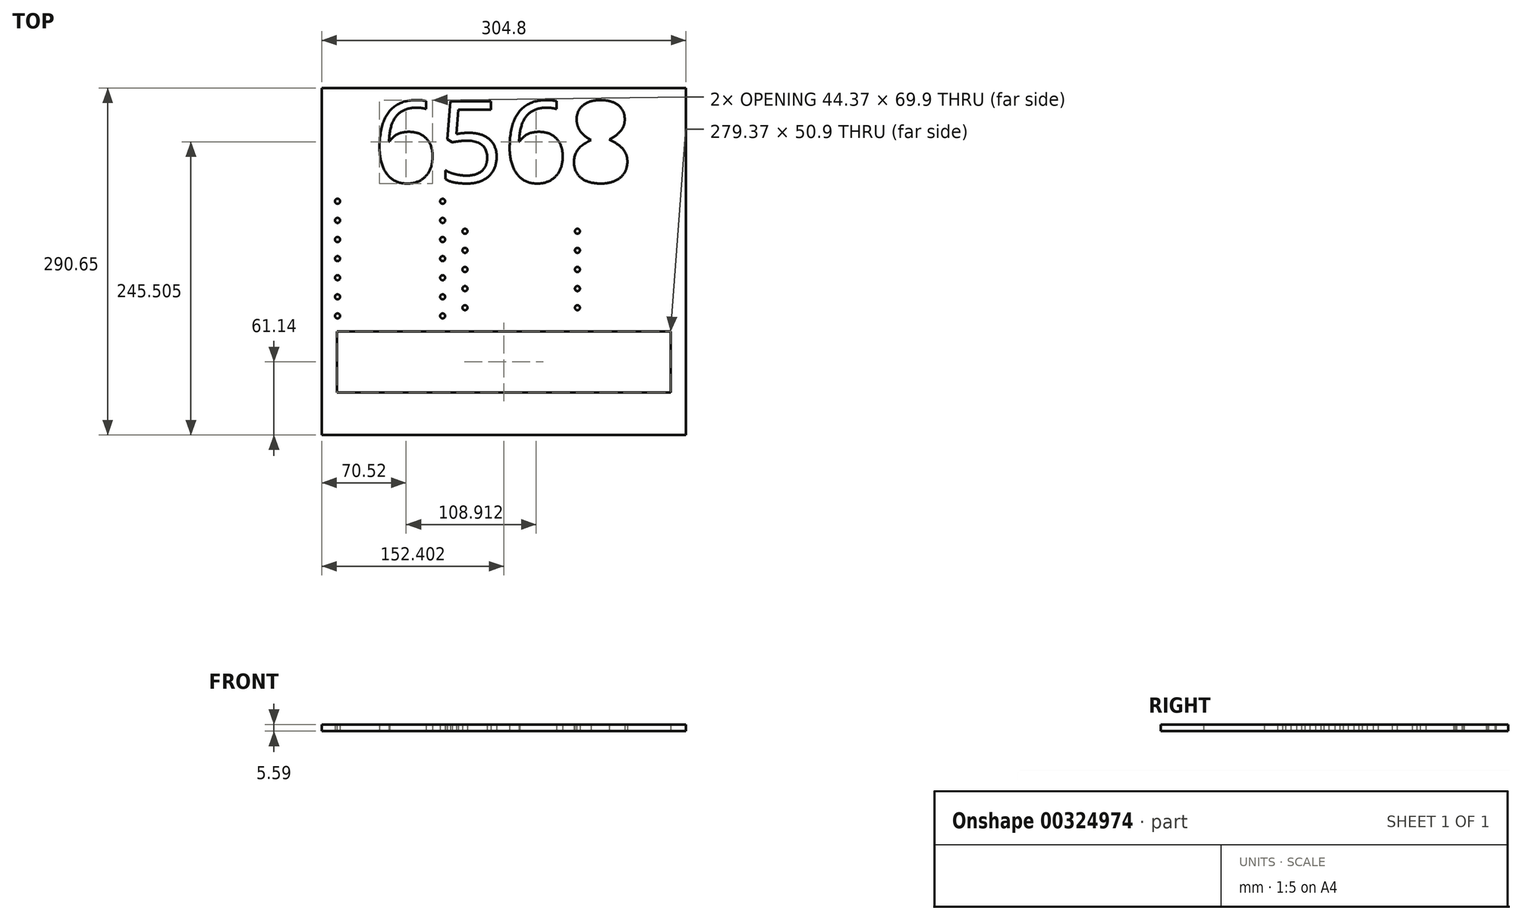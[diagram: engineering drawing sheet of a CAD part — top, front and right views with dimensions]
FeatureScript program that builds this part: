
annotation { "Feature Type Name" : "Feature", "Feature Type Description" : "" }
export const myFeature = defineFeature(function(context is Context, id is Id, definition is map)
    precondition{}
    {
        {
            var Q0;
            Q0=qCreatedBy(makeId("Top.planeOp"),FACE);
            var sketch = newSketch(context, id + "F0", { "sketchPlane" : qUnion([Q0])});
            skLineSegment(sketch, "E0.top", {"start": v(-150.79, -86.6) * mm, "end": v(154.01, -86.6) * mm});
            skLineSegment(sketch, "E0.left", {"start": v(-150.79, 204.06) * mm, "end": v(-150.79, -86.6) * mm});
            skLineSegment(sketch, "E0.right", {"start": v(154.01, 204.06) * mm, "end": v(154.01, -86.6) * mm});
            skLineSegment(sketch, "E1", {"start": v(-138.07, -50.9) * mm, "end": v(-138.07, 0) * mm});
            skLineSegment(sketch, "E2", {"start": v(141.3, -50.9) * mm, "end": v(141.3, 0) * mm});
            skLineSegment(sketch, "E3", {"start": v(-138.07, 0) * mm, "end": v(141.3, 0) * mm});
            skLineSegment(sketch, "E4", {"start": v(-138.07, -50.9) * mm, "end": v(141.3, -50.9) * mm});
            skCircle(sketch, "E5", {"center": v(-137.64, 13.08) * mm, "radius": 2.1 * mm});
            skPoint(sketch, "E5.first.point", {"position": v(-137.67, 15.18) * mm});
            skPoint(sketch, "E5.second.point", {"position": v(-135.54, 13.06) * mm});
            skPoint(sketch, "E5.third.point", {"position": v(-138.07, 11.03) * mm});
            skCircle(sketch, "E6", {"center": v(-137.64, 29.08) * mm, "radius": 2.1 * mm});
            skPoint(sketch, "E6.first.point", {"position": v(-137.68, 31.18) * mm});
            skPoint(sketch, "E6.second.point", {"position": v(-135.62, 28.5) * mm});
            skPoint(sketch, "E6.third.point", {"position": v(-139.13, 27.6) * mm});
            skCircle(sketch, "E7", {"center": v(-137.63, 45.09) * mm, "radius": 2.1 * mm});
            skPoint(sketch, "E7.first.point", {"position": v(-137.64, 47.18) * mm});
            skPoint(sketch, "E7.second.point", {"position": v(-138.72, 46.88) * mm});
            skPoint(sketch, "E7.third.point", {"position": v(-136.8, 43.16) * mm});
            skCircle(sketch, "E8", {"center": v(-137.63, 61.08) * mm, "radius": 2.1 * mm});
            skPoint(sketch, "E8.first.point", {"position": v(-137.63, 63.18) * mm});
            skPoint(sketch, "E8.second.point", {"position": v(-138.89, 62.76) * mm});
            skPoint(sketch, "E8.third.point", {"position": v(-136.93, 59.1) * mm});
            skCircle(sketch, "E9", {"center": v(-137.64, 77.07) * mm, "radius": 2.1 * mm});
            skPoint(sketch, "E9.first.point", {"position": v(-138.72, 78.88) * mm});
            skPoint(sketch, "E9.second.point", {"position": v(-139.12, 78.57) * mm});
            skPoint(sketch, "E9.third.point", {"position": v(-136.52, 75.3) * mm});
            skCircle(sketch, "E10", {"center": v(-137.63, 93.09) * mm, "radius": 2.1 * mm});
            skPoint(sketch, "E10.first.point", {"position": v(-139.31, 94.34) * mm});
            skPoint(sketch, "E10.second.point", {"position": v(-139.56, 93.92) * mm});
            skPoint(sketch, "E10.third.point", {"position": v(-136.07, 91.68) * mm});
            skCircle(sketch, "E11", {"center": v(-137.63, 109.11) * mm, "radius": 2.11 * mm});
            skPoint(sketch, "E11.first.point", {"position": v(-139.7, 108.7) * mm});
            skPoint(sketch, "E11.second.point", {"position": v(-139.64, 108.48) * mm});
            skPoint(sketch, "E11.third.point", {"position": v(-135.74, 108.18) * mm});
            skCircle(sketch, "E12", {"center": v(-49.63, 109.08) * mm, "radius": 2.1 * mm});
            skPoint(sketch, "E12.first.point", {"position": v(-50.34, 107.1) * mm});
            skPoint(sketch, "E12.second.point", {"position": v(-48.8, 107.15) * mm});
            skPoint(sketch, "E12.third.point", {"position": v(-49.24, 111.15) * mm});
            skCircle(sketch, "E13", {"center": v(-49.63, 93.08) * mm, "radius": 2.1 * mm});
            skPoint(sketch, "E13.first.point", {"position": v(-49.3, 95.16) * mm});
            skPoint(sketch, "E13.second.point", {"position": v(-51.64, 92.47) * mm});
            skPoint(sketch, "E13.third.point", {"position": v(-49.1, 91.05) * mm});
            skCircle(sketch, "E14", {"center": v(-49.63, 77.08) * mm, "radius": 2.1 * mm});
            skPoint(sketch, "E14.first.point", {"position": v(-49.56, 74.99) * mm});
            skPoint(sketch, "E14.second.point", {"position": v(-48.67, 78.95) * mm});
            skPoint(sketch, "E14.third.point", {"position": v(-51.72, 77.28) * mm});
            skCircle(sketch, "E15", {"center": v(-49.63, 61.08) * mm, "radius": 2.1 * mm});
            skPoint(sketch, "E15.first.point", {"position": v(-49.36, 63.17) * mm});
            skPoint(sketch, "E15.second.point", {"position": v(-47.7, 61.89) * mm});
            skPoint(sketch, "E15.third.point", {"position": v(-51.3, 59.81) * mm});
            skCircle(sketch, "E16", {"center": v(-49.63, 45.08) * mm, "radius": 2.1 * mm});
            skPoint(sketch, "E16.first.point", {"position": v(-49.58, 47.18) * mm});
            skPoint(sketch, "E16.second.point", {"position": v(-47.57, 45.49) * mm});
            skPoint(sketch, "E16.third.point", {"position": v(-49.93, 43) * mm});
            skCircle(sketch, "E17", {"center": v(-49.63, 29.08) * mm, "radius": 2.1 * mm});
            skPoint(sketch, "E17.first.point", {"position": v(-48.52, 30.87) * mm});
            skPoint(sketch, "E17.second.point", {"position": v(-51.47, 30.1) * mm});
            skPoint(sketch, "E17.third.point", {"position": v(-49.04, 27.07) * mm});
            skCircle(sketch, "E18", {"center": v(-49.63, 13.08) * mm, "radius": 2.1 * mm});
            skPoint(sketch, "E18.first.point", {"position": v(-48.44, 14.81) * mm});
            skPoint(sketch, "E18.second.point", {"position": v(-51.72, 12.9) * mm});
            skPoint(sketch, "E18.third.point", {"position": v(-49.41, 11) * mm});
            skCircle(sketch, "E19", {"center": v(-30.95, 83.97) * mm, "radius": 2.1 * mm});
            skPoint(sketch, "E19.first.point", {"position": v(-32.05, 85.77) * mm});
            skPoint(sketch, "E19.second.point", {"position": v(-31.38, 81.92) * mm});
            skPoint(sketch, "E19.third.point", {"position": v(-28.96, 84.64) * mm});
            skCircle(sketch, "E20", {"center": v(-30.95, 67.97) * mm, "radius": 2.1 * mm});
            skPoint(sketch, "E20.first.point", {"position": v(-30.95, 70.07) * mm});
            skPoint(sketch, "E20.second.point", {"position": v(-32.65, 66.74) * mm});
            skPoint(sketch, "E20.third.point", {"position": v(-29.85, 66.18) * mm});
            skCircle(sketch, "E21", {"center": v(-30.95, 51.97) * mm, "radius": 2.1 * mm});
            skPoint(sketch, "E21.first.point", {"position": v(-33.05, 51.97) * mm});
            skPoint(sketch, "E21.first.point.positionSnap0", {"position": v(-34.95, 51.97) * mm});
            skPoint(sketch, "E21.second.point", {"position": v(-29.85, 50.18) * mm});
            skPoint(sketch, "E21.third.point", {"position": v(-29.85, 53.76) * mm});
            skCircle(sketch, "E22", {"center": v(-30.95, 35.97) * mm, "radius": 2.1 * mm});
            skPoint(sketch, "E22.first.point", {"position": v(-32.98, 36.49) * mm});
            skPoint(sketch, "E22.second.point", {"position": v(-32.03, 34.17) * mm});
            skPoint(sketch, "E22.third.point", {"position": v(-29.85, 37.76) * mm});
            skCircle(sketch, "E23", {"center": v(-30.95, 19.97) * mm, "radius": 2.1 * mm});
            skPoint(sketch, "E23.first.point", {"position": v(-32.6, 21.27) * mm});
            skPoint(sketch, "E23.second.point", {"position": v(-30.95, 17.87) * mm});
            skPoint(sketch, "E23.third.point", {"position": v(-28.85, 19.97) * mm});
            skCircle(sketch, "E24", {"center": v(63.19, 83.97) * mm, "radius": 2.1 * mm});
            skPoint(sketch, "E24.first.point", {"position": v(62.1, 85.77) * mm});
            skPoint(sketch, "E24.second.point", {"position": v(62.76, 81.92) * mm});
            skPoint(sketch, "E24.third.point", {"position": v(65.18, 84.64) * mm});
            skCircle(sketch, "E25", {"center": v(63.19, 67.97) * mm, "radius": 2.1 * mm});
            skPoint(sketch, "E25.first.point", {"position": v(63.19, 70.07) * mm});
            skPoint(sketch, "E25.second.point", {"position": v(61.49, 66.74) * mm});
            skPoint(sketch, "E25.third.point", {"position": v(64.29, 66.18) * mm});
            skCircle(sketch, "E26", {"center": v(63.2, 51.97) * mm, "radius": 2.1 * mm});
            skPoint(sketch, "E26.first.point", {"position": v(61.1, 51.97) * mm});
            skPoint(sketch, "E26.first.point.positionSnap0", {"position": v(59.2, 51.97) * mm});
            skPoint(sketch, "E26.second.point", {"position": v(64.29, 50.18) * mm});
            skPoint(sketch, "E26.third.point", {"position": v(64.29, 53.76) * mm});
            skCircle(sketch, "E27", {"center": v(63.2, 35.97) * mm, "radius": 2.1 * mm});
            skPoint(sketch, "E27.first.point", {"position": v(61.16, 36.49) * mm});
            skPoint(sketch, "E27.second.point", {"position": v(62.1, 34.17) * mm});
            skPoint(sketch, "E27.third.point", {"position": v(64.29, 37.76) * mm});
            skCircle(sketch, "E28", {"center": v(63.2, 19.97) * mm, "radius": 2.1 * mm});
            skPoint(sketch, "E28.first.point", {"position": v(61.54, 21.27) * mm});
            skPoint(sketch, "E28.second.point", {"position": v(63.19, 17.87) * mm});
            skPoint(sketch, "E28.third.point", {"position": v(65.3, 19.97) * mm});
            skText(sketch, "E29", { "text": "6568", "fontName": "OpenSans-Regular.ttf"});
            skLineSegment(sketch, "E30", {"start": v(-150.79, 204.06) * mm, "end": v(154.01, 204.06) * mm});
            const initialGuessF0  = {"E29": [-0.1079, 0.1249, 1, 0, 0.06858]};
            skSetInitialGuess(sketch, initialGuessF0);
            skSolve(sketch);
        }
        {
            var Q0;
            Q0=makeQuery(id+"F0.imprint","IMPRINT",FACE,{"disambiguationData":[TD([[makeQuery(id+"F0.imprint","IMPRINT",EDGE,{"derivedFrom":sQuery(id+"F0.wireOp",EDGE,"E0.top")}),1.0]])]});
            extrude(context, id + "F1", {"entities" : qUnion([Q0]), "depth" : 5.6 * mm});
        }
    });
